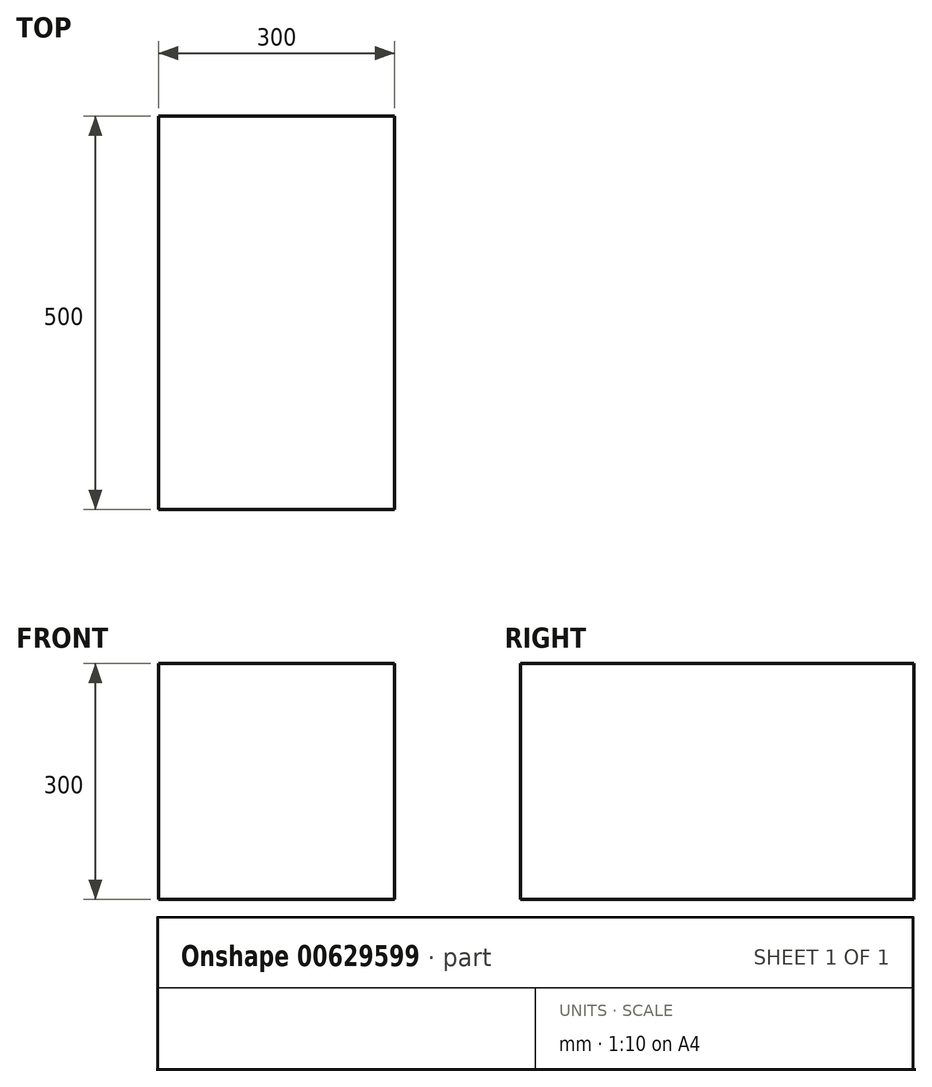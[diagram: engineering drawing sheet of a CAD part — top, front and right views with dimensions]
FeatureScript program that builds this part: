
annotation { "Feature Type Name" : "Feature", "Feature Type Description" : "" }
export const myFeature = defineFeature(function(context is Context, id is Id, definition is map)
    precondition{}
    {
        {
            var Q0;
            Q0=qCreatedBy(makeId("Front.planeOp"),FACE);
            var sketch = newSketch(context, id + "F0", { "sketchPlane" : qUnion([Q0])});
            skLineSegment(sketch, "E0.bottom", {"start": v(150, 150) * mm, "end": v(-150, 150) * mm});
            skLineSegment(sketch, "E0.top", {"start": v(150, -150) * mm, "end": v(-150, -150) * mm});
            skLineSegment(sketch, "E0.left", {"start": v(150, 150) * mm, "end": v(150, -150) * mm});
            skLineSegment(sketch, "E0.right", {"start": v(-150, 150) * mm, "end": v(-150, -150) * mm});
            skPoint(sketch, "E0.middle", {"position": v(0, 0) * mm});
            skSolve(sketch);
        }
        {
            var Q0;
            Q0=makeQuery(id+"F0.imprint","IMPRINT",FACE,{"disambiguationData":[TD([[makeQuery(id+"F0.imprint","IMPRINT",EDGE,{"derivedFrom":sQuery(id+"F0.wireOp",EDGE,"E0.bottom")}),1.0]])]});
            extrude(context, id + "F1", {"entities" : qUnion([Q0]), "oppositeDirection" : true, "depth" : 500 * mm, "offsetDistance" : 25 * mm});
        }
    });
